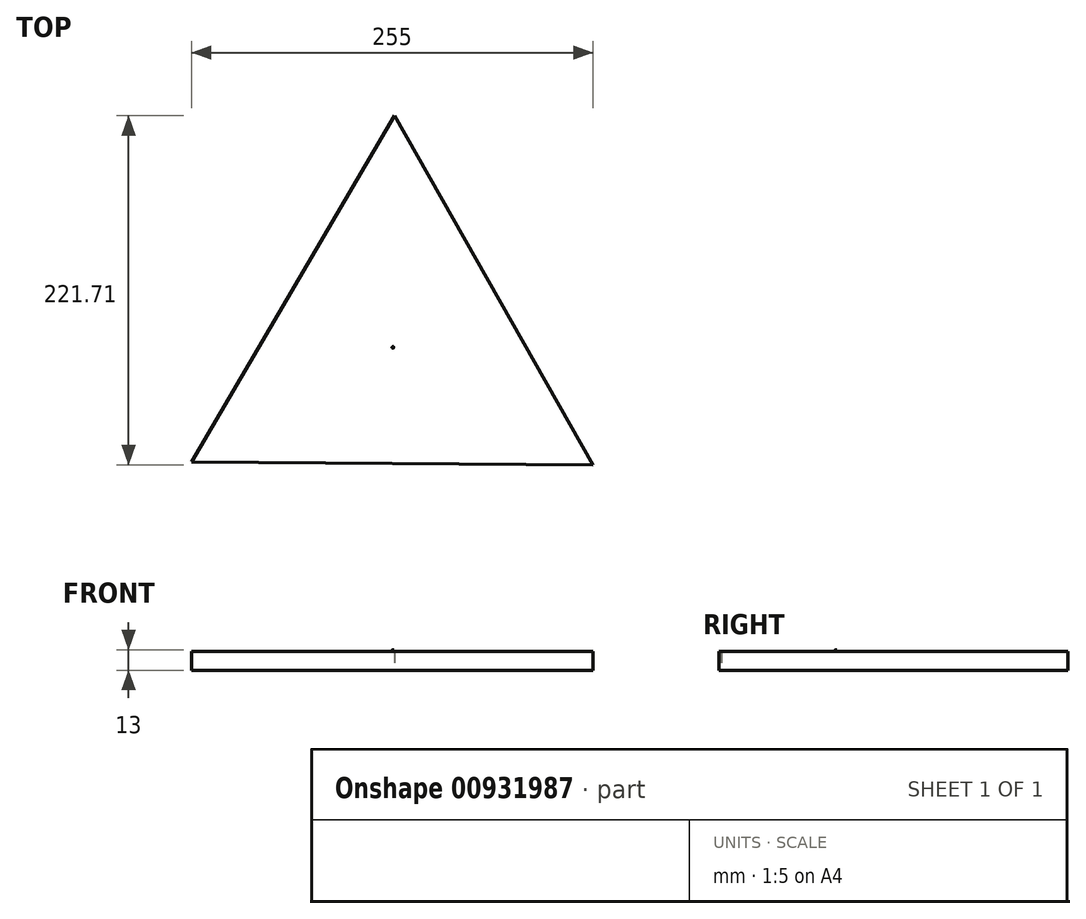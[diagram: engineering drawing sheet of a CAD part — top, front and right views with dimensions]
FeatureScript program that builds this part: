
annotation { "Feature Type Name" : "Feature", "Feature Type Description" : "" }
export const myFeature = defineFeature(function(context is Context, id is Id, definition is map)
    precondition{}
    {
        {
            var Q0;
            Q0=qCreatedBy(makeId("Top.planeOp"),FACE);
            var sketch = newSketch(context, id + "F0", { "sketchPlane" : qUnion([Q0])});
            skCircle(sketch, "E0.cCircle", {"center": v(0, 0) * mm, "radius": 73.61 * mm, "construction": true});
            skLineSegment(sketch, "E0.0", {"start": v(1.02, 147.22) * mm, "end": v(126.99, -74.5) * mm});
            skLineSegment(sketch, "E0.1", {"start": v(126.99, -74.5) * mm, "end": v(-128, -72.73) * mm});
            skLineSegment(sketch, "E0.2", {"start": v(-128, -72.73) * mm, "end": v(1.02, 147.22) * mm});
            skPoint(sketch, "E0.0.midPoint", {"position": v(64, 36.36) * mm});
            skSolve(sketch);
        }
        {
            var Q0;
            Q0=makeQuery(id+"F0.imprint","IMPRINT",FACE,{"disambiguationData":[TD([[makeQuery(id+"F0.imprint","IMPRINT",EDGE,{"derivedFrom":sQuery(id+"F0.wireOp",EDGE,"E0.0")}),-1.0]])]});
            extrude(context, id + "F1", {"entities" : qUnion([Q0]), "depth" : 12 * mm, "offsetDistance" : 25 * mm});
        }
        {
            var Q0;
            Q0=makeQuery(id+"F1.opExtrude","CAP_FACE",FACE,{"disambiguationData":[OSD([sQuery(id+"F0.wireOp",EDGE,"E0.0"),sQuery(id+"F0.wireOp",EDGE,"E0.1"),sQuery(id+"F0.wireOp",EDGE,"E0.2")])],"isStart":false});
            var sketch = newSketch(context, id + "F2", { "sketchPlane" : qUnion([Q0])});
            skCircle(sketch, "E1", {"center": v(0, 0) * mm, "radius": 0.5 * mm});
            skSolve(sketch);
        }
        {
            var Q0;
            Q0 = qSketchRegion(id + "F2", true);
            extrude(context, id + "F3", {"entities" : qUnion([Q0]), "operationType" : NewBodyOperationType.ADD, "depth" : 1 * mm, "offsetDistance" : 25 * mm});
        }
    });
